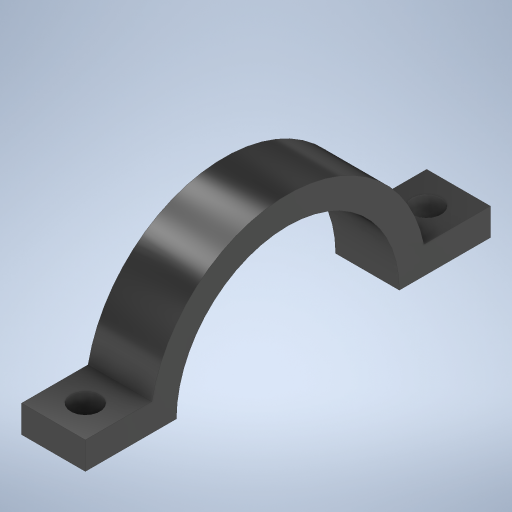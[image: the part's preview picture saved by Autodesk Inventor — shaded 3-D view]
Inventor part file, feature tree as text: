
AUTODESK INVENTOR PART (.ipt)
format: ipt  version: 2023 (Build 270158000, 158)  size: 271,872 bytes
history: native  units: mm
features: sketch x3, extrude x2, hole x1, mirror x1
ambient origin geometry x8: Origin, YZ Plane, XZ Plane, XY Plane, X Axis, Y Axis, Z Axis, Center Point
bodies: Volumenkörper1 (feature_tree)
feature tree (7):
  extrude  "Extrusion1"  TaperAngle=180.0deg  [1 undecoded]
  extrude  "Extrusion3"  Depth=7.0mm TaperAngle=0.0deg
  hole  "Bohrung1"  [1 undecoded]
  mirror  "Spiegeln1"
  sketch  "Skizze1"  dims[d0=12.25mm d1=180.0deg]
  sketch  "Skizze3"  dims[d3=15.25mm d4=7.0mm d5=0.0mm]
  sketch  "Skizze5"  dims[d6=7.0mm d7=3.0mm d10=7.0mm d11=0.0mm d12=3.2mm d13=6.0mm d14=4.0mm d15=2.0mm d16=90.0deg d17=8.0mm d18=20.594885mm d19=3.5mm d20=3.5mm]
note: 2 required parameter values undecoded (feature->parameter linkage not recoverable at this tier; creation-order binding heuristic only, values carry confidence <= 0.55)
